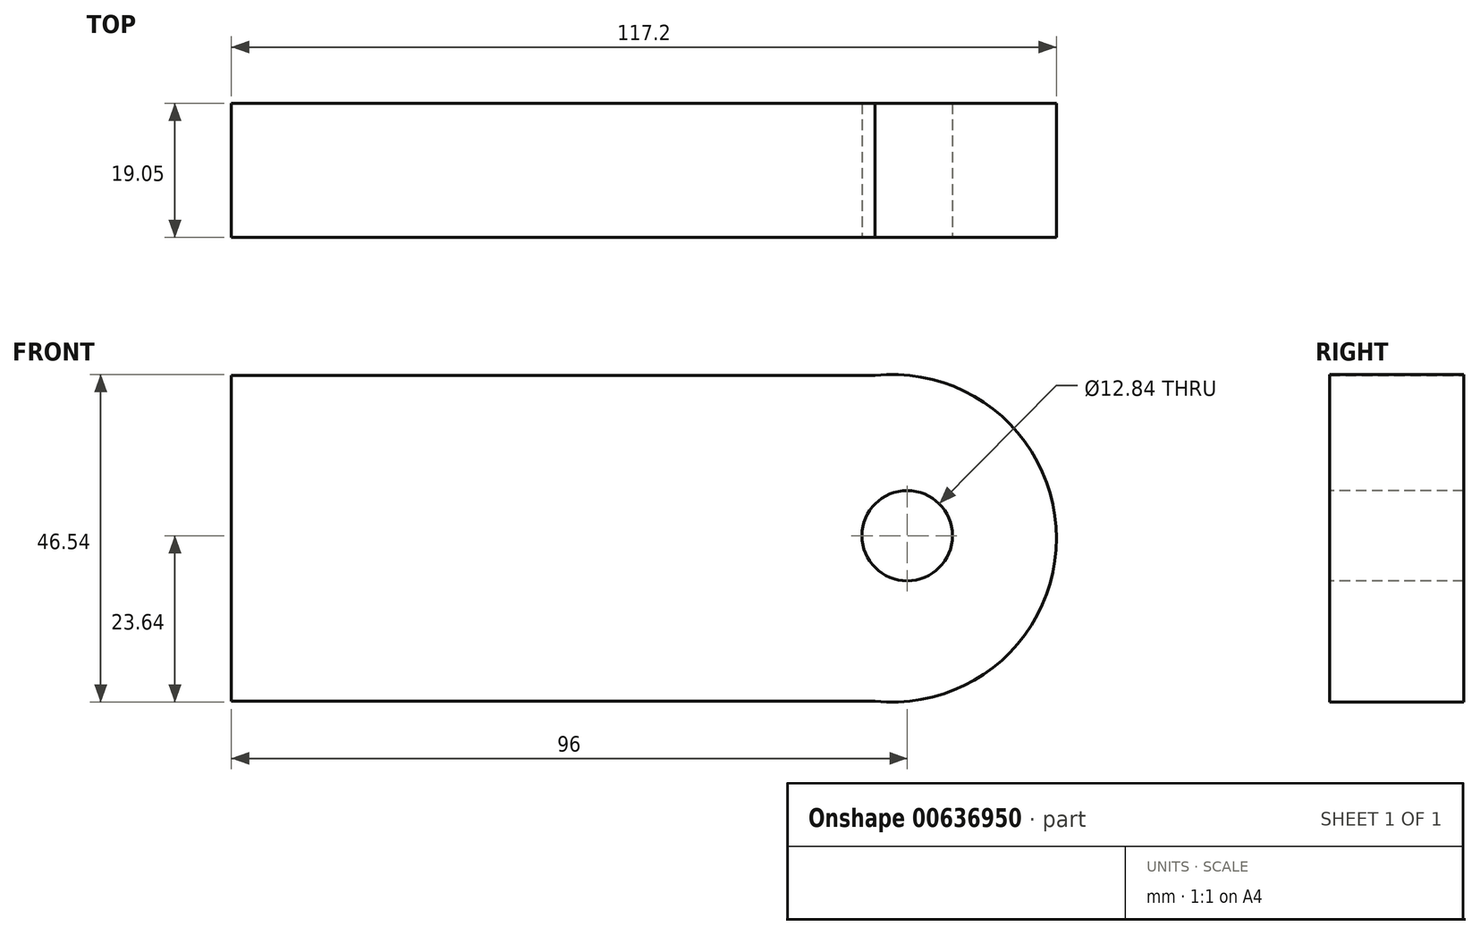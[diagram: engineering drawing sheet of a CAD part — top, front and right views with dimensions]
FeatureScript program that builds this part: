
annotation { "Feature Type Name" : "Feature", "Feature Type Description" : "" }
export const myFeature = defineFeature(function(context is Context, id is Id, definition is map)
    precondition{}
    {
        {
            var Q0;
            Q0=qCreatedBy(makeId("Front.planeOp"),FACE);
            var sketch = newSketch(context, id + "F0", { "sketchPlane" : qUnion([Q0])});
            skLineSegment(sketch, "E0", {"start": v(-60.74, -23.5) * mm, "end": v(30.7, -23.5) * mm});
            skLineSegment(sketch, "E1", {"start": v(30.7, -23.5) * mm, "end": v(30.7, 22.77) * mm});
            skLineSegment(sketch, "E2", {"start": v(30.7, 22.77) * mm, "end": v(-60.74, 22.77) * mm});
            skLineSegment(sketch, "E3", {"start": v(-60.74, 22.77) * mm, "end": v(-60.74, -23.5) * mm});
            skArc(sketch, "E4", {"start": v(30.7, -23.5) * mm, "mid": v(56.46, -0.37) * mm, "end": v(30.7, 22.77) * mm});
            skSolve(sketch);
        }
        {
            var Q0;
            Q0 = qSketchRegion(id + "F0", true);
            extrude(context, id + "F1", {"entities" : qUnion([Q0]), "depth" : 19.05 * mm, "offsetDistance" : 25.4 * mm});
        }
        {
            var Q0;
            Q0=makeQuery(id+"F1.opExtrude","CAP_FACE",FACE,{"disambiguationData":[OSD([sQuery(id+"F0.wireOp",EDGE,"E0"),sQuery(id+"F0.wireOp",EDGE,"E2"),sQuery(id+"F0.wireOp",EDGE,"E3"),sQuery(id+"F0.wireOp",EDGE,"E4")])],"isStart":false});
            var sketch = newSketch(context, id + "F2", { "sketchPlane" : qUnion([Q0])});
            skCircle(sketch, "E5", {"center": v(35.26, 0) * mm, "radius": 6.42 * mm});
            skSolve(sketch);
        }
        {
            var Q0;
            Q0=makeQuery(id+"F2.imprint","IMPRINT",FACE,{"disambiguationData":[TD([[makeQuery(id+"F2.imprint","IMPRINT",EDGE,{"derivedFrom":sQuery(id+"F2.wireOp",EDGE,"E5")}),1.0]])]});
            extrude(context, id + "F3", {"entities" : qUnion([Q0]), "operationType" : NewBodyOperationType.REMOVE, "oppositeDirection" : true, "depth" : 70.36 * mm, "offsetDistance" : 25.4 * mm});
        }
    });
